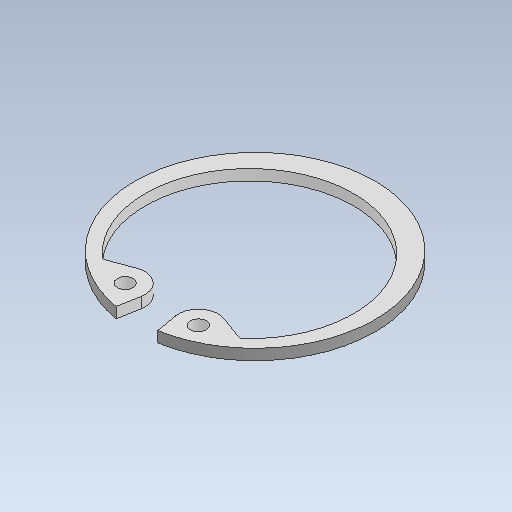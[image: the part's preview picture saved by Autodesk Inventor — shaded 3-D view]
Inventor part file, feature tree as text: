
AUTODESK INVENTOR PART (.ipt)
format: ipt  version: 2020 (Build 240168000, 168)  size: 104,448 bytes
history: native  units: in
note: dims shown in document units (in); Inventor stores cm internally (conversion verified against a paired STEP export)
features: fillet x1
ambient origin geometry x8: Origin, YZ Plane, XZ Plane, XY Plane, X Axis, Y Axis, Z Axis, Center Point
bodies: Solid1 (feature_tree)
feature tree (1):
  fillet  "Fillet1"  [1 undecoded]
note: 1 required parameter value undecoded (feature->parameter linkage not recoverable at this tier; creation-order binding heuristic only, values carry confidence <= 0.55)
